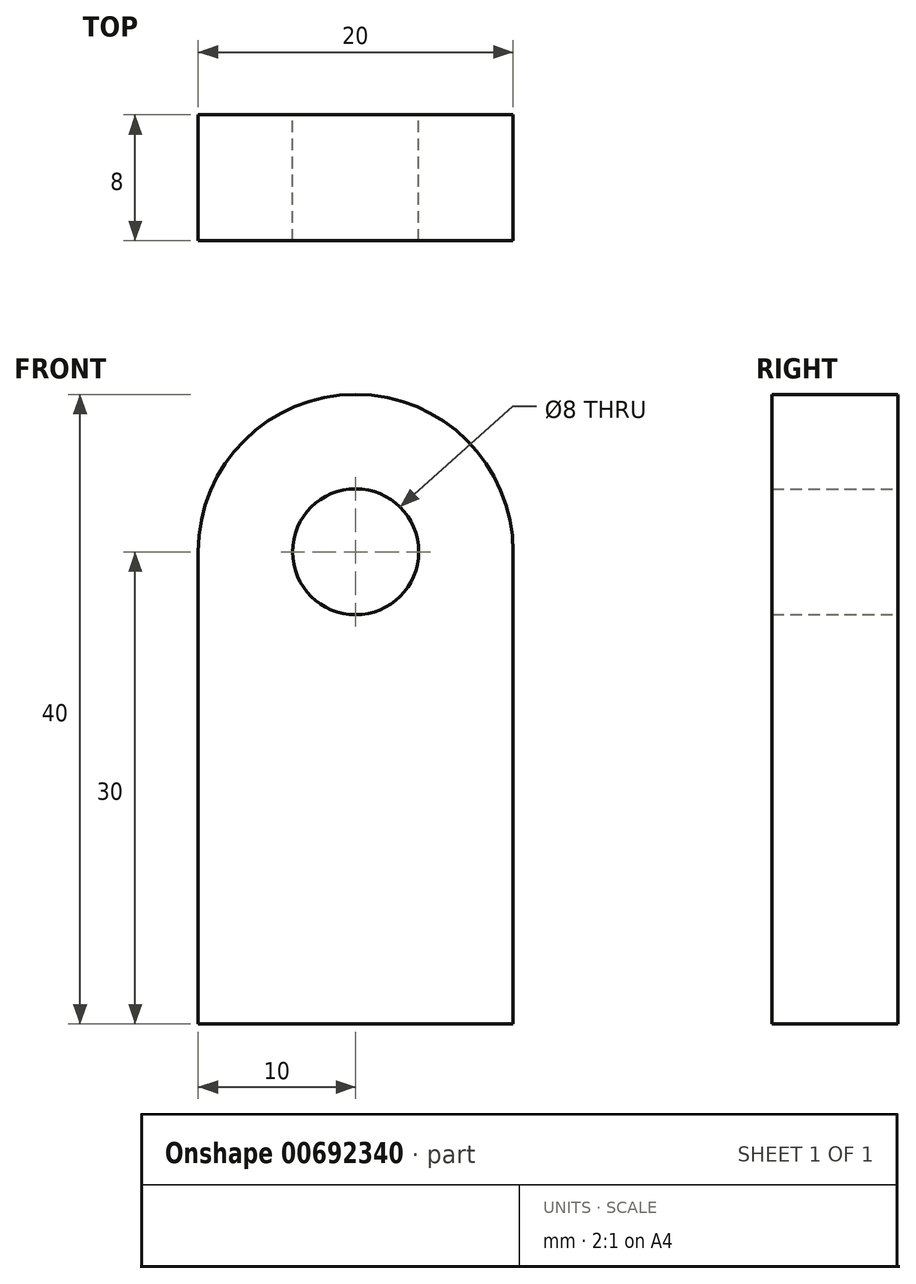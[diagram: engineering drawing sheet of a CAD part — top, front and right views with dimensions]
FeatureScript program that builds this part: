
annotation { "Feature Type Name" : "Feature", "Feature Type Description" : "" }
export const myFeature = defineFeature(function(context is Context, id is Id, definition is map)
    precondition{}
    {
        {
            var Q0;
            Q0=qCreatedBy(makeId("Front.planeOp"),FACE);
            var sketch = newSketch(context, id + "F0", { "sketchPlane" : qUnion([Q0])});
            skCircle(sketch, "E0", {"center": v(0, 30) * mm, "radius": 4 * mm});
            skArc(sketch, "E1", {"start": v(10, 30) * mm, "mid": v(0, 40) * mm, "end": v(-10, 30) * mm});
            skLineSegment(sketch, "E2", {"start": v(-13.77, 30) * mm, "end": v(14.75, 30) * mm, "construction": true});
            skLineSegment(sketch, "E3", {"start": v(-10, 30) * mm, "end": v(-10, 0) * mm});
            skLineSegment(sketch, "E4", {"start": v(10, 30) * mm, "end": v(10, 0) * mm});
            skLineSegment(sketch, "E5", {"start": v(-10, 0) * mm, "end": v(10, 0) * mm});
            skSolve(sketch);
        }
        {
            var Q0;
            Q0 = qSketchRegion(id + "F0", true);
            extrude(context, id + "F1", {"entities" : qUnion([Q0]), "depth" : 8 * mm, "offsetDistance" : 25 * mm});
        }
    });
